# Revit family: BDG_BossDesign_Tbls_Myriad
name_source: partatom
category: Furniture
revit_build: Autodesk Revit 2015 (Build: 20140903_1530(x64)
units: mm (PartAtom-declared; Revit-internal decimal feet)

## types (1)
- Square Coffee Table
    Assembly Code = E2020200
    AssetType = Movable
    BIMObjectName = BDG_BossDesign_Tables_Myriad
    Category = Pr_40_50_21_14 : Coffee tables
    CodePerformance = BSEN 16139:2013
    Color = White
    Description = Square Coffee Table
    DurationUnit = year
    ExpectedLife = 5
    IfcExportAs = IfcFurnishingElementType
    IfcExportType = TABLE
    Keynote = Pr_40_50_21_14
    MainColor = White
    ManufacturerName = Boss Design
    ManufacturerURL = www.bossdesign.com
    Material = MFC
    Model = MYR/CT
    ModelNumber = MYR/CT
    ModelReference = Square Coffee Table
    NBSDescription = Tables
    NBSReference = 45-35-86/327
    Name = Tables_Myriad_BossDesign
    NominalHeight = 345 mm  [stored 1.13189 ft]
    NominalLength = 670 mm  [stored 2.19816 ft]
    NominalWidth = 670 mm  [stored 2.19816 ft]
    NumberOfChairs = 0
    ProductInformation = www.bossdesign.com/product-list/myriad/
    Shape = Square
    Size = 670 x 670 x 345mm
    SustainabilityPerformance = 99% Recyclable
    URL = www.bossdesign.com
    Uniclass2015Code = Pr_40_50_21_14
    Uniclass2015Title = Coffee tables
    Uniclass2015Version = Products v1.10
    Version = 1
    WarrantyDescription = Structural Warranty Excludes Foams and Fabrics
    WarrantyDurationLabor = 5
    WarrantyDurationParts = 5
    WarrantyDurationUnit = year
    WorksurfaceArea = 0.45 m²

note: [stored X ft] marks values corroborated as IEEE doubles in the binary element streams (Revit-internal decimal feet)

## geometry (parser evidence)
native form markers: Sweep x3
no freeform markers — native parametric forms only
